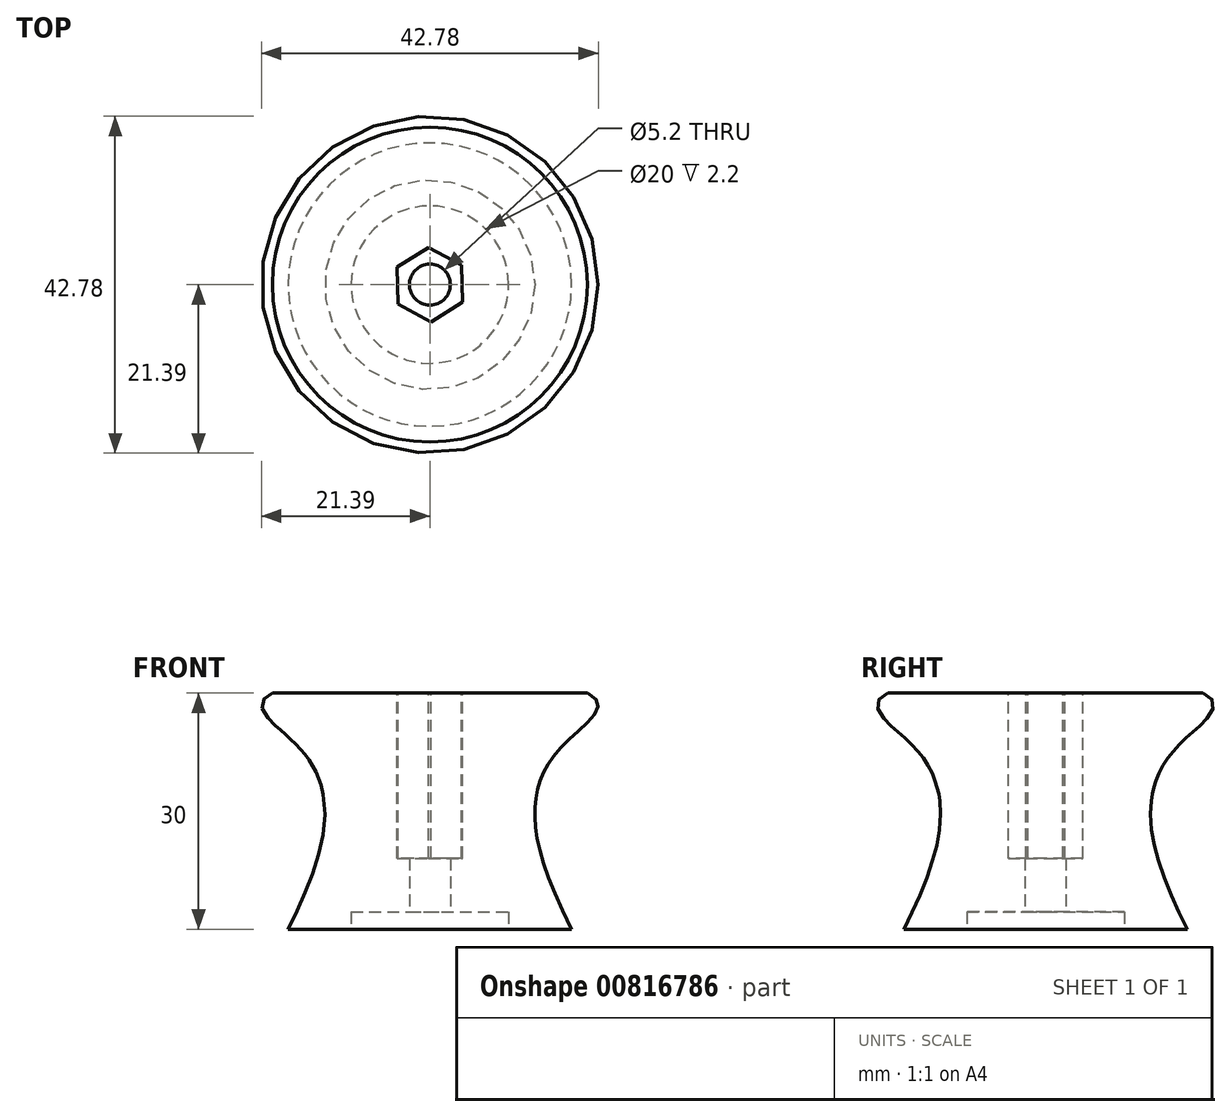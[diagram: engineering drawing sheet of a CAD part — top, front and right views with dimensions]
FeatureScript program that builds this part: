
annotation { "Feature Type Name" : "Feature", "Feature Type Description" : "" }
export const myFeature = defineFeature(function(context is Context, id is Id, definition is map)
    precondition{}
    {
        {
            var Q0;
            Q0=qCreatedBy(makeId("Front.planeOp"),FACE);
            var sketch = newSketch(context, id + "F0", { "sketchPlane" : qUnion([Q0])});
            skLineSegment(sketch, "E0", {"start": v(0, 0) * mm, "end": v(18, 0) * mm});
            skLineSegment(sketch, "E1", {"start": v(0, 30) * mm, "end": v(20, 30) * mm});
            skFitSpline(sketch, "E2", {"points": [v(20, 30) * mm, v(17.53, 23.99) * mm, v(13.47, 16.56) * mm, v(18, 0) * mm], "startDerivative": vector(38.04, -16.61) * mm, "endDerivative": vector(28.87, -57.49) * mm});
            skLineSegment(sketch, "E3", {"start": v(0, 30) * mm, "end": v(0, 0) * mm});
            skSolve(sketch);
        }
        {
            var Q0;
            Q0=makeQuery(id+"F0.imprint","IMPRINT",FACE,{"disambiguationData":[TD([[makeQuery(id+"F0.imprint","IMPRINT",EDGE,{"derivedFrom":sQuery(id+"F0.wireOp",EDGE,"E0")}),1.0]])]});
            var Q1;
            Q1=sQuery(id+"F0.wireOp",EDGE,"E3");
            revolve(context, id + "F1", {"surfaceOperationType" : NewSurfaceOperationType.NEW, "entities" : qUnion([Q0]), "axis" : qUnion([Q1]), "revolveType" : RevolveType.FULL});
        }
        {
            var Q0;
            Q0=makeQuery(id+"F1.opRevolve","SWEPT_FACE",FACE,{"disambiguationData":[OSD([sQuery(id+"F0.wireOp",EDGE,"E0")])]});
            var sketch = newSketch(context, id + "F2", { "sketchPlane" : qUnion([Q0])});
            skCircle(sketch, "E4", {"center": v(0, 0) * mm, "radius": 10 * mm});
            skSolve(sketch);
        }
        {
            var Q0;
            Q0 = qSketchRegion(id + "F2", true);
            extrude(context, id + "F3", {"entities" : qUnion([Q0]), "operationType" : NewBodyOperationType.REMOVE, "oppositeDirection" : true, "depth" : 2.2 * mm, "offsetDistance" : 25 * mm});
        }
        {
            var Q0;
            Q0=makeQuery(id+"F3.boolean.opBoolean","COPY",FACE,{"derivedFrom":makeQuery(id+"F3.opExtrude","CAP_FACE",FACE,{"disambiguationData":[OSD([sQuery(id+"F2.wireOp",EDGE,"E4")])],"isStart":false})});
            var sketch = newSketch(context, id + "F4", { "sketchPlane" : qUnion([Q0])});
            skCircle(sketch, "E5", {"center": v(0, 0) * mm, "radius": 2.6 * mm});
            skSolve(sketch);
        }
        {
            var Q0;
            Q0 = qSketchRegion(id + "F4", true);
            extrude(context, id + "F5", {"entities" : qUnion([Q0]), "operationType" : NewBodyOperationType.REMOVE, "endBound" : BoundingType.THROUGH_ALL, "oppositeDirection" : true, "depth" : 25 * mm, "offsetDistance" : 25 * mm});
        }
        {
            var Q0;
            Q0=qCreatedBy(makeId("Top.planeOp"),FACE);
            cPlane(context, id + "F6", {"entities" : qUnion([Q0]), "cplaneType" : CPlaneType.OFFSET, "offset" : 13 * mm, "width" : 150 * mm, "height" : 150 * mm});
        }
        {
            var Q0;
            Q0=qCreatedBy(id+"F6.planeOp",FACE);
            var sketch = newSketch(context, id + "F7", { "sketchPlane" : qUnion([Q0])});
            skCircle(sketch, "E6.cCircle", {"center": v(0, 0) * mm, "radius": 4.1 * mm, "construction": true});
            skLineSegment(sketch, "E6.0", {"start": v(-0.15, 4.73) * mm, "end": v(4.02, 2.5) * mm});
            skLineSegment(sketch, "E6.1", {"start": v(4.02, 2.5) * mm, "end": v(4.17, -2.23) * mm});
            skLineSegment(sketch, "E6.2", {"start": v(4.17, -2.23) * mm, "end": v(0.15, -4.73) * mm});
            skLineSegment(sketch, "E6.3", {"start": v(0.15, -4.73) * mm, "end": v(-4.02, -2.5) * mm});
            skLineSegment(sketch, "E6.4", {"start": v(-4.02, -2.5) * mm, "end": v(-4.17, 2.23) * mm});
            skLineSegment(sketch, "E6.5", {"start": v(-4.17, 2.23) * mm, "end": v(-0.15, 4.73) * mm});
            skPoint(sketch, "E6.0.midPoint", {"position": v(1.93, 3.61) * mm});
            skSolve(sketch);
        }
        {
            var Q0;
            Q0 = qSketchRegion(id + "F7", true);
            extrude(context, id + "F8", {"entities" : qUnion([Q0]), "operationType" : NewBodyOperationType.REMOVE, "oppositeDirection" : true, "depth" : 4 * mm, "offsetDistance" : 25 * mm, "hasSecondDirection" : true, "secondDirectionOppositeDirection" : false, "secondDirectionDepth" : 25 * mm});
        }
    });
